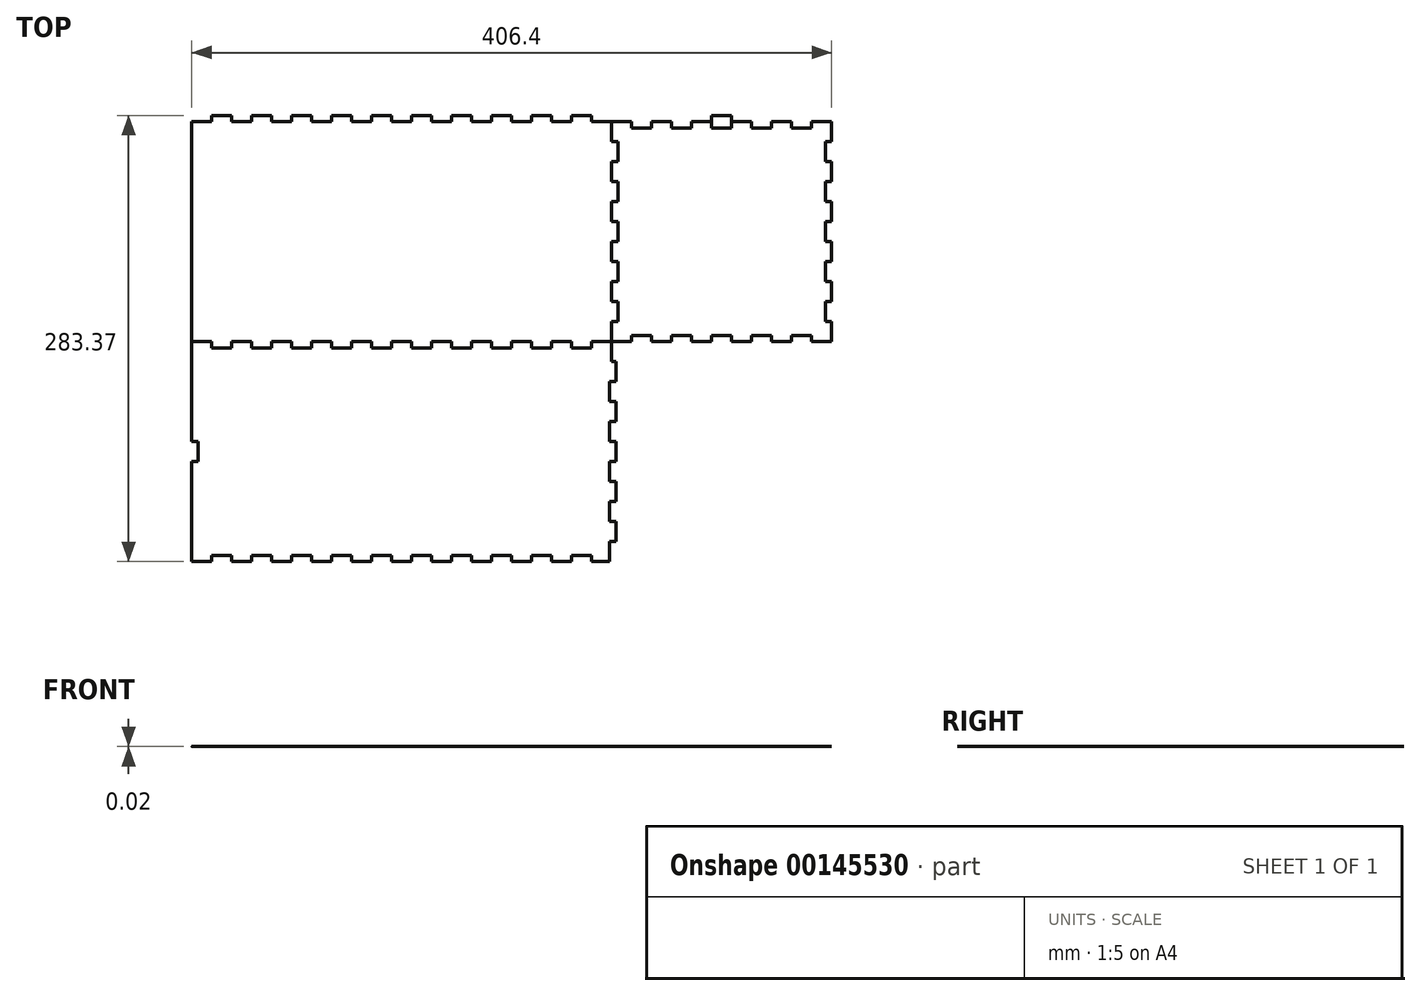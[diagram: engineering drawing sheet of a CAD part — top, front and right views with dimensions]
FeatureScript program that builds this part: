
annotation { "Feature Type Name" : "Feature", "Feature Type Description" : "" }
export const myFeature = defineFeature(function(context is Context, id is Id, definition is map)
    precondition{}
    {
        {
            var Q0;
            Q0=qCreatedBy(makeId("Top.planeOp"),FACE);
            var sketch = newSketch(context, id + "F0", { "sketchPlane" : qUnion([Q0])});
            skLineSegment(sketch, "E0", {"start": v(70.3, -71.79) * mm, "end": v(70.3, -59.09) * mm});
            skLineSegment(sketch, "E1.top", {"start": v(57.6, -67.82) * mm, "end": v(57.6, -71.79) * mm});
            skLineSegment(sketch, "E1.right", {"start": v(70.3, -71.79) * mm, "end": v(57.6, -71.79) * mm});
            skLineSegment(sketch, "E2.0.1.1", {"start": v(44.9, -67.82) * mm, "end": v(44.9, -71.79) * mm});
            skLineSegment(sketch, "E2.0.1.2", {"start": v(44.9, -71.79) * mm, "end": v(32.2, -71.79) * mm});
            skLineSegment(sketch, "E2.0.1.3", {"start": v(32.2, -67.82) * mm, "end": v(32.2, -71.79) * mm});
            skLineSegment(sketch, "E2.0.2.1", {"start": v(19.5, -67.82) * mm, "end": v(19.5, -71.79) * mm});
            skLineSegment(sketch, "E2.0.2.2", {"start": v(19.5, -71.79) * mm, "end": v(6.8, -71.79) * mm});
            skLineSegment(sketch, "E2.0.2.3", {"start": v(6.8, -67.82) * mm, "end": v(6.8, -71.79) * mm});
            skLineSegment(sketch, "E2.0.3.1", {"start": v(-5.9, -67.82) * mm, "end": v(-5.9, -71.79) * mm});
            skLineSegment(sketch, "E2.0.3.2", {"start": v(-5.9, -71.79) * mm, "end": v(-18.6, -71.79) * mm});
            skLineSegment(sketch, "E2.0.3.3", {"start": v(-18.6, -67.82) * mm, "end": v(-18.6, -71.79) * mm});
            skLineSegment(sketch, "E2.0.4.1", {"start": v(-31.3, -67.82) * mm, "end": v(-31.3, -71.79) * mm});
            skLineSegment(sketch, "E2.0.4.2", {"start": v(-31.3, -71.79) * mm, "end": v(-44, -71.79) * mm});
            skLineSegment(sketch, "E2.0.4.3", {"start": v(-44, -67.82) * mm, "end": v(-44, -71.79) * mm});
            skLineSegment(sketch, "E3", {"start": v(-44, -67.82) * mm, "end": v(-56.7, -67.82) * mm});
            skLineSegment(sketch, "E4", {"start": v(-31.3, -67.82) * mm, "end": v(-18.6, -67.82) * mm});
            skLineSegment(sketch, "E5", {"start": v(-5.9, -67.82) * mm, "end": v(6.8, -67.82) * mm});
            skLineSegment(sketch, "E6", {"start": v(19.5, -67.82) * mm, "end": v(32.2, -67.82) * mm});
            skLineSegment(sketch, "E7", {"start": v(44.9, -67.82) * mm, "end": v(57.6, -67.82) * mm});
            skLineSegment(sketch, "E8.MirrorCS", {"start": v(70.3, -46.39) * mm, "end": v(70.3, -33.69) * mm});
            skLineSegment(sketch, "E9.MirrorCS", {"start": v(66.34, -46.39) * mm, "end": v(66.34, -59.09) * mm});
            skLineSegment(sketch, "E10.MirrorCS", {"start": v(70.3, -33.69) * mm, "end": v(66.34, -33.69) * mm});
            skLineSegment(sketch, "E11.MirrorCS", {"start": v(66.34, -20.99) * mm, "end": v(66.34, -33.69) * mm});
            skLineSegment(sketch, "E12.MirrorCS", {"start": v(70.3, 4.41) * mm, "end": v(66.34, 4.41) * mm});
            skLineSegment(sketch, "E13.MirrorCS", {"start": v(70.3, 29.81) * mm, "end": v(66.34, 29.81) * mm});
            skLineSegment(sketch, "E14.MirrorCS", {"start": v(70.3, -46.39) * mm, "end": v(66.34, -46.39) * mm});
            skLineSegment(sketch, "E15.MirrorCS", {"start": v(70.3, 29.81) * mm, "end": v(70.3, 42.51) * mm});
            skLineSegment(sketch, "E16.MirrorCS", {"start": v(70.3, -20.99) * mm, "end": v(66.34, -20.99) * mm});
            skLineSegment(sketch, "E17.MirrorCS", {"start": v(66.34, 29.81) * mm, "end": v(66.34, 17.11) * mm});
            skLineSegment(sketch, "E18.MirrorCS", {"start": v(70.3, 42.51) * mm, "end": v(66.34, 42.51) * mm});
            skLineSegment(sketch, "E19.MirrorCS", {"start": v(70.3, 17.11) * mm, "end": v(66.34, 17.11) * mm});
            skLineSegment(sketch, "E20.MirrorCS", {"start": v(70.3, 55.21) * mm, "end": v(66.34, 55.21) * mm});
            skLineSegment(sketch, "E21.MirrorCS", {"start": v(70.3, -8.29) * mm, "end": v(66.34, -8.29) * mm});
            skLineSegment(sketch, "E22.MirrorCS", {"start": v(70.3, -59.09) * mm, "end": v(66.34, -59.09) * mm});
            skLineSegment(sketch, "E23.MirrorCS", {"start": v(70.3, 4.41) * mm, "end": v(70.3, 17.11) * mm});
            skLineSegment(sketch, "E24.MirrorCS", {"start": v(66.34, 55.21) * mm, "end": v(66.34, 42.51) * mm});
            skLineSegment(sketch, "E25.MirrorCS", {"start": v(66.34, 4.41) * mm, "end": v(66.34, -8.29) * mm});
            skLineSegment(sketch, "E26.MirrorCS", {"start": v(70.3, -20.99) * mm, "end": v(70.3, -8.29) * mm});
            skLineSegment(sketch, "E27", {"start": v(70.3, 67.91) * mm, "end": v(70.3, 55.21) * mm});
            skLineSegment(sketch, "E28.MirrorCS", {"start": v(70.3, -33.69) * mm, "end": v(70.3, -46.39) * mm});
            skLineSegment(sketch, "E29.MirrorCS", {"start": v(66.34, 42.51) * mm, "end": v(66.34, 55.21) * mm});
            skLineSegment(sketch, "E30.MirrorCS", {"start": v(66.34, 17.11) * mm, "end": v(66.34, 29.81) * mm});
            skLineSegment(sketch, "E31.MirrorCS", {"start": v(66.34, -33.69) * mm, "end": v(66.34, -20.99) * mm});
            skLineSegment(sketch, "E32.MirrorCS", {"start": v(70.3, -8.29) * mm, "end": v(70.3, -20.99) * mm});
            skLineSegment(sketch, "E33.MirrorCS", {"start": v(66.34, -8.29) * mm, "end": v(66.34, 4.41) * mm});
            skLineSegment(sketch, "E34.MirrorCS", {"start": v(70.3, 17.11) * mm, "end": v(70.3, 4.41) * mm});
            skLineSegment(sketch, "E35.MirrorCS", {"start": v(66.34, -59.09) * mm, "end": v(66.34, -46.39) * mm});
            skLineSegment(sketch, "E36.MirrorCS", {"start": v(70.3, 42.51) * mm, "end": v(70.3, 29.81) * mm});
            skLineSegment(sketch, "E37", {"start": v(-56.7, -67.82) * mm, "end": v(-56.7, -71.79) * mm});
            skLineSegment(sketch, "E38", {"start": v(-56.7, -71.79) * mm, "end": v(-69.4, -71.79) * mm});
            skLineSegment(sketch, "E39.MirrorCS", {"start": v(-69.4, 17.11) * mm, "end": v(-65.42, 17.11) * mm});
            skLineSegment(sketch, "E40.MirrorCS", {"start": v(-69.4, 29.81) * mm, "end": v(-65.42, 29.81) * mm});
            skLineSegment(sketch, "E41.MirrorCS", {"start": v(-69.4, -33.69) * mm, "end": v(-65.42, -33.69) * mm});
            skLineSegment(sketch, "E42.MirrorCS", {"start": v(-69.4, 42.51) * mm, "end": v(-65.42, 42.51) * mm});
            skLineSegment(sketch, "E43.MirrorCS", {"start": v(-69.4, -8.29) * mm, "end": v(-65.42, -8.29) * mm});
            skLineSegment(sketch, "E44.MirrorCS", {"start": v(-69.4, -46.39) * mm, "end": v(-65.42, -46.39) * mm});
            skLineSegment(sketch, "E45.MirrorCS", {"start": v(-69.4, -20.99) * mm, "end": v(-65.42, -20.99) * mm});
            skLineSegment(sketch, "E46.MirrorCS", {"start": v(-69.4, 4.41) * mm, "end": v(-65.42, 4.41) * mm});
            skLineSegment(sketch, "E47.MirrorCS", {"start": v(-69.4, -59.09) * mm, "end": v(-65.42, -59.09) * mm});
            skLineSegment(sketch, "E48.MirrorCS", {"start": v(-69.4, 55.21) * mm, "end": v(-65.42, 55.21) * mm});
            skLineSegment(sketch, "E49.MirrorCS", {"start": v(-69.4, -8.29) * mm, "end": v(-69.4, -20.99) * mm});
            skLineSegment(sketch, "E50.MirrorCS", {"start": v(-69.4, -46.39) * mm, "end": v(-69.4, -33.69) * mm});
            skLineSegment(sketch, "E51.MirrorCS", {"start": v(-65.42, -59.09) * mm, "end": v(-65.42, -46.39) * mm});
            skLineSegment(sketch, "E52.MirrorCS", {"start": v(-69.4, -71.79) * mm, "end": v(-69.4, -59.09) * mm});
            skLineSegment(sketch, "E53.MirrorCS", {"start": v(-69.4, 29.81) * mm, "end": v(-69.4, 42.51) * mm});
            skLineSegment(sketch, "E54.MirrorCS", {"start": v(-65.42, -8.29) * mm, "end": v(-65.42, 4.41) * mm});
            skLineSegment(sketch, "E55.MirrorCS", {"start": v(-65.42, -20.99) * mm, "end": v(-65.42, -33.69) * mm});
            skLineSegment(sketch, "E56.MirrorCS", {"start": v(-65.42, 29.81) * mm, "end": v(-65.42, 17.11) * mm});
            skLineSegment(sketch, "E57.MirrorCS", {"start": v(-69.4, 4.41) * mm, "end": v(-69.4, 17.11) * mm});
            skLineSegment(sketch, "E58.MirrorCS", {"start": v(-69.4, 67.91) * mm, "end": v(-69.4, 55.21) * mm});
            skLineSegment(sketch, "E59.MirrorCS", {"start": v(-65.42, 42.51) * mm, "end": v(-65.42, 55.21) * mm});
            skLineSegment(sketch, "E60.MirrorCS", {"start": v(-69.4, -33.69) * mm, "end": v(-69.4, -46.39) * mm});
            skLineSegment(sketch, "E61.MirrorCS", {"start": v(-69.4, 17.11) * mm, "end": v(-69.4, 4.41) * mm});
            skLineSegment(sketch, "E62.MirrorCS", {"start": v(-65.42, 4.41) * mm, "end": v(-65.42, -8.29) * mm});
            skLineSegment(sketch, "E63.MirrorCS", {"start": v(-69.4, 42.51) * mm, "end": v(-69.4, 29.81) * mm});
            skLineSegment(sketch, "E64.MirrorCS", {"start": v(-65.42, 17.11) * mm, "end": v(-65.42, 29.81) * mm});
            skLineSegment(sketch, "E65.MirrorCS", {"start": v(-69.4, -20.99) * mm, "end": v(-69.4, -8.29) * mm});
            skLineSegment(sketch, "E66.MirrorCS", {"start": v(-65.42, 55.21) * mm, "end": v(-65.42, 42.51) * mm});
            skLineSegment(sketch, "E67.MirrorCS", {"start": v(-65.42, -33.69) * mm, "end": v(-65.42, -20.99) * mm});
            skLineSegment(sketch, "E68.MirrorCS", {"start": v(-65.42, -46.39) * mm, "end": v(-65.42, -59.09) * mm});
            skLineSegment(sketch, "E69.MirrorCS", {"start": v(-69.4, -71.79) * mm, "end": v(-56.7, -71.79) * mm});
            skLineSegment(sketch, "E70.MirrorCS", {"start": v(-31.3, 63.95) * mm, "end": v(-31.3, 67.91) * mm});
            skLineSegment(sketch, "E71.MirrorCS", {"start": v(-5.9, 63.95) * mm, "end": v(-5.9, 67.91) * mm});
            skLineSegment(sketch, "E72.MirrorCS", {"start": v(6.8, 63.95) * mm, "end": v(6.8, 67.91) * mm});
            skLineSegment(sketch, "E73.MirrorCS", {"start": v(-44, 63.95) * mm, "end": v(-44, 67.91) * mm});
            skLineSegment(sketch, "E74.MirrorCS", {"start": v(57.6, 63.95) * mm, "end": v(57.6, 67.91) * mm});
            skLineSegment(sketch, "E75.MirrorCS", {"start": v(32.2, 63.95) * mm, "end": v(32.2, 67.91) * mm});
            skLineSegment(sketch, "E76.MirrorCS", {"start": v(19.5, 63.95) * mm, "end": v(19.5, 67.91) * mm});
            skLineSegment(sketch, "E77.MirrorCS", {"start": v(44.9, 63.95) * mm, "end": v(44.9, 67.91) * mm});
            skLineSegment(sketch, "E78.MirrorCS", {"start": v(-56.7, 63.95) * mm, "end": v(-56.7, 67.91) * mm});
            skLineSegment(sketch, "E79.MirrorCS", {"start": v(-18.6, 63.95) * mm, "end": v(-18.6, 67.91) * mm});
            skLineSegment(sketch, "E80.MirrorCS", {"start": v(-56.7, 67.91) * mm, "end": v(-69.4, 67.91) * mm});
            skLineSegment(sketch, "E81.MirrorCS", {"start": v(-69.4, 67.91) * mm, "end": v(-56.7, 67.91) * mm});
            skLineSegment(sketch, "E82.MirrorCS", {"start": v(-44, 63.95) * mm, "end": v(-56.7, 63.95) * mm});
            skLineSegment(sketch, "E83.MirrorCS", {"start": v(-31.3, 67.91) * mm, "end": v(-44, 67.91) * mm});
            skLineSegment(sketch, "E84.MirrorCS", {"start": v(44.9, 63.95) * mm, "end": v(57.6, 63.95) * mm});
            skLineSegment(sketch, "E85.MirrorCS", {"start": v(-5.9, 67.91) * mm, "end": v(-18.6, 67.91) * mm});
            skLineSegment(sketch, "E86.MirrorCS", {"start": v(19.5, 63.95) * mm, "end": v(32.2, 63.95) * mm});
            skLineSegment(sketch, "E87.MirrorCS", {"start": v(44.9, 67.91) * mm, "end": v(32.2, 67.91) * mm});
            skLineSegment(sketch, "E88.MirrorCS", {"start": v(70.3, 67.91) * mm, "end": v(57.6, 67.91) * mm});
            skLineSegment(sketch, "E89.MirrorCS", {"start": v(-31.3, 63.95) * mm, "end": v(-18.6, 63.95) * mm});
            skLineSegment(sketch, "E90.MirrorCS", {"start": v(-5.9, 63.95) * mm, "end": v(6.8, 63.95) * mm});
            skLineSegment(sketch, "E91.MirrorCS", {"start": v(19.5, 67.91) * mm, "end": v(6.8, 67.91) * mm});
            skSolve(sketch);
        }
        {
            var Q0;
            Q0 = qSketchRegion(id + "F0", true);
            extrude(context, id + "F1", {"entities" : qUnion([Q0]), "depth" : 5 / 812.8 * mm});
        }
        {
            var Q0;
            Q0=makeQuery(id+"F1.opExtrude","CAP_FACE",FACE,{"disambiguationData":[OSD([sQuery(id+"F0.wireOp",EDGE,"E0"),sQuery(id+"F0.wireOp",EDGE,"E1.top"),sQuery(id+"F0.wireOp",EDGE,"E1.right"),sQuery(id+"F0.wireOp",EDGE,"E2.0.1.1"),sQuery(id+"F0.wireOp",EDGE,"E2.0.1.2"),sQuery(id+"F0.wireOp",EDGE,"E2.0.1.3"),sQuery(id+"F0.wireOp",EDGE,"E2.0.2.1"),sQuery(id+"F0.wireOp",EDGE,"E2.0.2.2"),sQuery(id+"F0.wireOp",EDGE,"E2.0.2.3"),sQuery(id+"F0.wireOp",EDGE,"E2.0.3.1"),sQuery(id+"F0.wireOp",EDGE,"E2.0.3.2"),sQuery(id+"F0.wireOp",EDGE,"E2.0.3.3"),sQuery(id+"F0.wireOp",EDGE,"E2.0.4.1"),sQuery(id+"F0.wireOp",EDGE,"E2.0.4.2"),sQuery(id+"F0.wireOp",EDGE,"E2.0.4.3"),sQuery(id+"F0.wireOp",EDGE,"E3"),sQuery(id+"F0.wireOp",EDGE,"E4"),sQuery(id+"F0.wireOp",EDGE,"E5"),sQuery(id+"F0.wireOp",EDGE,"E6"),sQuery(id+"F0.wireOp",EDGE,"E7"),sQuery(id+"F0.wireOp",EDGE,"E27"),sQuery(id+"F0.wireOp",EDGE,"E28.MirrorCS"),sQuery(id+"F0.wireOp",EDGE,"E21.MirrorCS"),sQuery(id+"F0.wireOp",EDGE,"E14.MirrorCS"),sQuery(id+"F0.wireOp",EDGE,"E29.MirrorCS"),sQuery(id+"F0.wireOp",EDGE,"E30.MirrorCS"),sQuery(id+"F0.wireOp",EDGE,"E31.MirrorCS"),sQuery(id+"F0.wireOp",EDGE,"E13.MirrorCS"),sQuery(id+"F0.wireOp",EDGE,"E20.MirrorCS"),sQuery(id+"F0.wireOp",EDGE,"E10.MirrorCS"),sQuery(id+"F0.wireOp",EDGE,"E32.MirrorCS"),sQuery(id+"F0.wireOp",EDGE,"E19.MirrorCS"),sQuery(id+"F0.wireOp",EDGE,"E33.MirrorCS"),sQuery(id+"F0.wireOp",EDGE,"E22.MirrorCS"),sQuery(id+"F0.wireOp",EDGE,"E12.MirrorCS"),sQuery(id+"F0.wireOp",EDGE,"E34.MirrorCS"),sQuery(id+"F0.wireOp",EDGE,"E16.MirrorCS"),sQuery(id+"F0.wireOp",EDGE,"E35.MirrorCS"),sQuery(id+"F0.wireOp",EDGE,"E36.MirrorCS"),sQuery(id+"F0.wireOp",EDGE,"E18.MirrorCS"),sQuery(id+"F0.wireOp",EDGE,"E37"),sQuery(id+"F0.wireOp",EDGE,"E45.MirrorCS"),sQuery(id+"F0.wireOp",EDGE,"E41.MirrorCS"),sQuery(id+"F0.wireOp",EDGE,"E43.MirrorCS"),sQuery(id+"F0.wireOp",EDGE,"E40.MirrorCS"),sQuery(id+"F0.wireOp",EDGE,"E44.MirrorCS"),sQuery(id+"F0.wireOp",EDGE,"E39.MirrorCS"),sQuery(id+"F0.wireOp",EDGE,"E42.MirrorCS"),sQuery(id+"F0.wireOp",EDGE,"E46.MirrorCS"),sQuery(id+"F0.wireOp",EDGE,"E47.MirrorCS"),sQuery(id+"F0.wireOp",EDGE,"E48.MirrorCS"),sQuery(id+"F0.wireOp",EDGE,"E52.MirrorCS"),sQuery(id+"F0.wireOp",EDGE,"E58.MirrorCS"),sQuery(id+"F0.wireOp",EDGE,"E60.MirrorCS"),sQuery(id+"F0.wireOp",EDGE,"E61.MirrorCS"),sQuery(id+"F0.wireOp",EDGE,"E62.MirrorCS"),sQuery(id+"F0.wireOp",EDGE,"E63.MirrorCS"),sQuery(id+"F0.wireOp",EDGE,"E64.MirrorCS"),sQuery(id+"F0.wireOp",EDGE,"E65.MirrorCS"),sQuery(id+"F0.wireOp",EDGE,"E66.MirrorCS"),sQuery(id+"F0.wireOp",EDGE,"E67.MirrorCS"),sQuery(id+"F0.wireOp",EDGE,"E68.MirrorCS"),sQuery(id+"F0.wireOp",EDGE,"E69.MirrorCS"),sQuery(id+"F0.wireOp",EDGE,"E70.MirrorCS"),sQuery(id+"F0.wireOp",EDGE,"E71.MirrorCS"),sQuery(id+"F0.wireOp",EDGE,"E72.MirrorCS"),sQuery(id+"F0.wireOp",EDGE,"E73.MirrorCS"),sQuery(id+"F0.wireOp",EDGE,"E74.MirrorCS"),sQuery(id+"F0.wireOp",EDGE,"E75.MirrorCS"),sQuery(id+"F0.wireOp",EDGE,"E76.MirrorCS"),sQuery(id+"F0.wireOp",EDGE,"E77.MirrorCS"),sQuery(id+"F0.wireOp",EDGE,"E78.MirrorCS"),sQuery(id+"F0.wireOp",EDGE,"E79.MirrorCS"),sQuery(id+"F0.wireOp",EDGE,"E81.MirrorCS"),sQuery(id+"F0.wireOp",EDGE,"E82.MirrorCS"),sQuery(id+"F0.wireOp",EDGE,"E83.MirrorCS"),sQuery(id+"F0.wireOp",EDGE,"E84.MirrorCS"),sQuery(id+"F0.wireOp",EDGE,"E85.MirrorCS"),sQuery(id+"F0.wireOp",EDGE,"E86.MirrorCS"),sQuery(id+"F0.wireOp",EDGE,"E87.MirrorCS"),sQuery(id+"F0.wireOp",EDGE,"E88.MirrorCS"),sQuery(id+"F0.wireOp",EDGE,"E89.MirrorCS"),sQuery(id+"F0.wireOp",EDGE,"E90.MirrorCS"),sQuery(id+"F0.wireOp",EDGE,"E91.MirrorCS")])],"isStart":true});
            var sketch = newSketch(context, id + "F2", { "sketchPlane" : qUnion([Q0])});
            skLineSegment(sketch, "E92.0", {"start": v(-69.4, -67.91) * mm, "end": v(-69.4, -55.21) * mm});
            skLineSegment(sketch, "E92.1", {"start": v(-69.4, -55.21) * mm, "end": v(-65.42, -55.21) * mm});
            skLineSegment(sketch, "E92.2", {"start": v(-65.42, -55.21) * mm, "end": v(-65.42, -42.51) * mm});
            skLineSegment(sketch, "E92.3", {"start": v(-69.4, -42.51) * mm, "end": v(-65.42, -42.51) * mm});
            skLineSegment(sketch, "E92.4", {"start": v(-69.4, -42.51) * mm, "end": v(-69.4, -29.81) * mm});
            skLineSegment(sketch, "E92.5", {"start": v(-69.4, -29.81) * mm, "end": v(-65.42, -29.81) * mm});
            skLineSegment(sketch, "E92.6", {"start": v(-65.42, -17.11) * mm, "end": v(-65.42, -29.81) * mm});
            skLineSegment(sketch, "E92.7", {"start": v(-69.4, -17.11) * mm, "end": v(-65.42, -17.11) * mm});
            skLineSegment(sketch, "E92.8", {"start": v(-69.4, -17.11) * mm, "end": v(-69.4, -4.41) * mm});
            skLineSegment(sketch, "E92.9", {"start": v(-69.4, -4.41) * mm, "end": v(-65.42, -4.41) * mm});
            skLineSegment(sketch, "E92.10", {"start": v(-65.42, -4.41) * mm, "end": v(-65.42, 8.29) * mm});
            skLineSegment(sketch, "E92.11", {"start": v(-69.4, 46.39) * mm, "end": v(-65.42, 46.39) * mm});
            skLineSegment(sketch, "E92.12", {"start": v(-65.42, 46.39) * mm, "end": v(-65.42, 59.09) * mm});
            skLineSegment(sketch, "E92.13", {"start": v(-69.4, 59.09) * mm, "end": v(-65.42, 59.09) * mm});
            skLineSegment(sketch, "E92.14", {"start": v(-69.4, 71.79) * mm, "end": v(-69.4, 59.09) * mm});
            skLineSegment(sketch, "E92.15", {"start": v(-69.4, 33.69) * mm, "end": v(-69.4, 46.39) * mm});
            skLineSegment(sketch, "E92.16", {"start": v(-69.4, 33.69) * mm, "end": v(-65.42, 33.69) * mm});
            skLineSegment(sketch, "E92.17", {"start": v(-65.42, 33.69) * mm, "end": v(-65.42, 20.99) * mm});
            skLineSegment(sketch, "E92.18", {"start": v(-69.4, 20.99) * mm, "end": v(-65.42, 20.99) * mm});
            skLineSegment(sketch, "E92.19", {"start": v(-69.4, 20.99) * mm, "end": v(-69.4, 8.29) * mm});
            skLineSegment(sketch, "E92.20", {"start": v(-69.4, 8.29) * mm, "end": v(-65.42, 8.29) * mm});
            skLineSegment(sketch, "E93.right", {"start": v(-336.1, 71.79) * mm, "end": v(-336.1, -67.91) * mm});
            skLineSegment(sketch, "E94.1.0.0", {"start": v(-132.9, -67.91) * mm, "end": v(-132.9, -71.88) * mm});
            skLineSegment(sketch, "E94.1.0.1", {"start": v(-107.5, -67.91) * mm, "end": v(-107.5, -71.88) * mm});
            skLineSegment(sketch, "E94.1.0.2", {"start": v(-107.5, -71.88) * mm, "end": v(-120.2, -71.88) * mm});
            skLineSegment(sketch, "E94.1.0.3", {"start": v(-82.1, -67.91) * mm, "end": v(-82.1, -71.88) * mm});
            skLineSegment(sketch, "E94.1.0.4", {"start": v(-107.5, -67.91) * mm, "end": v(-94.8, -67.91) * mm});
            skLineSegment(sketch, "E94.1.0.6", {"start": v(-196.4, -67.91) * mm, "end": v(-196.4, -71.88) * mm});
            skLineSegment(sketch, "E94.1.0.7", {"start": v(-196.4, -71.88) * mm, "end": v(-183.7, -71.88) * mm});
            skLineSegment(sketch, "E94.1.0.8", {"start": v(-183.7, -67.91) * mm, "end": v(-183.7, -71.88) * mm});
            skLineSegment(sketch, "E94.1.0.9", {"start": v(-183.7, -67.91) * mm, "end": v(-171, -67.91) * mm});
            skLineSegment(sketch, "E94.1.0.10", {"start": v(-171, -67.91) * mm, "end": v(-171, -71.88) * mm});
            skLineSegment(sketch, "E94.1.0.11", {"start": v(-158.3, -71.88) * mm, "end": v(-171, -71.88) * mm});
            skLineSegment(sketch, "E94.1.0.12", {"start": v(-158.3, -67.91) * mm, "end": v(-158.3, -71.88) * mm});
            skLineSegment(sketch, "E94.1.0.13", {"start": v(-158.3, -67.91) * mm, "end": v(-145.6, -67.91) * mm});
            skLineSegment(sketch, "E94.1.0.14", {"start": v(-145.6, -71.88) * mm, "end": v(-132.9, -71.88) * mm});
            skLineSegment(sketch, "E94.1.0.15", {"start": v(-145.6, -67.91) * mm, "end": v(-145.6, -71.88) * mm});
            skLineSegment(sketch, "E94.1.0.16", {"start": v(-94.8, -67.91) * mm, "end": v(-94.8, -71.88) * mm});
            skLineSegment(sketch, "E94.1.0.17", {"start": v(-94.8, -71.88) * mm, "end": v(-82.1, -71.88) * mm});
            skLineSegment(sketch, "E94.1.0.18", {"start": v(-120.2, -67.91) * mm, "end": v(-120.2, -71.88) * mm});
            skLineSegment(sketch, "E94.1.0.19", {"start": v(-120.2, -67.91) * mm, "end": v(-132.9, -67.91) * mm});
            skLineSegment(sketch, "E95", {"start": v(-69.4, -67.91) * mm, "end": v(-82.1, -67.91) * mm});
            skLineSegment(sketch, "E96", {"start": v(-209.1, 71.79) * mm, "end": v(-202.74, 71.79) * mm});
            skLineSegment(sketch, "E97.MirrorCS", {"start": v(-323.4, -67.91) * mm, "end": v(-323.4, -71.88) * mm});
            skLineSegment(sketch, "E98.MirrorCS", {"start": v(-247.2, -67.91) * mm, "end": v(-247.2, -71.88) * mm});
            skLineSegment(sketch, "E99.MirrorCS", {"start": v(-298, -67.91) * mm, "end": v(-298, -71.88) * mm});
            skLineSegment(sketch, "E100.MirrorCS", {"start": v(-272.6, -67.91) * mm, "end": v(-272.6, -71.88) * mm});
            skLineSegment(sketch, "E101.MirrorCS", {"start": v(-234.5, -67.91) * mm, "end": v(-234.5, -71.88) * mm});
            skLineSegment(sketch, "E102.MirrorCS", {"start": v(-285.3, -67.91) * mm, "end": v(-285.3, -71.88) * mm});
            skLineSegment(sketch, "E103.MirrorCS", {"start": v(-259.9, -67.91) * mm, "end": v(-259.9, -71.88) * mm});
            skLineSegment(sketch, "E104.MirrorCS", {"start": v(-221.8, -67.91) * mm, "end": v(-221.8, -71.88) * mm});
            skLineSegment(sketch, "E105.MirrorCS", {"start": v(-310.7, -67.91) * mm, "end": v(-310.7, -71.88) * mm});
            skLineSegment(sketch, "E106.MirrorCS", {"start": v(-209.1, -67.91) * mm, "end": v(-209.1, -71.88) * mm});
            skLineSegment(sketch, "E107.MirrorCS", {"start": v(-336.1, -67.91) * mm, "end": v(-323.4, -67.91) * mm});
            skLineSegment(sketch, "E108.MirrorCS", {"start": v(-209.1, -71.88) * mm, "end": v(-221.8, -71.88) * mm});
            skLineSegment(sketch, "E109.MirrorCS", {"start": v(-285.3, -67.91) * mm, "end": v(-272.6, -67.91) * mm});
            skLineSegment(sketch, "E110.MirrorCS", {"start": v(-298, -71.88) * mm, "end": v(-285.3, -71.88) * mm});
            skLineSegment(sketch, "E111.MirrorCS", {"start": v(-247.2, -67.91) * mm, "end": v(-259.9, -67.91) * mm});
            skLineSegment(sketch, "E112.MirrorCS", {"start": v(-298, -67.91) * mm, "end": v(-310.7, -67.91) * mm});
            skLineSegment(sketch, "E113.MirrorCS", {"start": v(-310.7, -71.88) * mm, "end": v(-323.4, -71.88) * mm});
            skLineSegment(sketch, "E114.MirrorCS", {"start": v(-247.2, -71.88) * mm, "end": v(-234.5, -71.88) * mm});
            skLineSegment(sketch, "E115.MirrorCS", {"start": v(-259.9, -71.88) * mm, "end": v(-272.6, -71.88) * mm});
            skLineSegment(sketch, "E116.MirrorCS", {"start": v(-221.8, -67.91) * mm, "end": v(-234.5, -67.91) * mm});
            skLineSegment(sketch, "E117", {"start": v(-209.1, -67.91) * mm, "end": v(-196.4, -67.91) * mm});
            skLineSegment(sketch, "E118.MirrorCS", {"start": v(-209.1, 71.79) * mm, "end": v(-209.1, 75.75) * mm});
            skLineSegment(sketch, "E119.MirrorCS", {"start": v(-94.8, 71.79) * mm, "end": v(-94.8, 75.75) * mm});
            skLineSegment(sketch, "E120.MirrorCS", {"start": v(-183.7, 71.79) * mm, "end": v(-183.7, 75.75) * mm});
            skLineSegment(sketch, "E121.MirrorCS", {"start": v(-298, 71.79) * mm, "end": v(-298, 75.75) * mm});
            skLineSegment(sketch, "E122.MirrorCS", {"start": v(-145.6, 71.79) * mm, "end": v(-145.6, 75.75) * mm});
            skLineSegment(sketch, "E123.MirrorCS", {"start": v(-158.3, 71.79) * mm, "end": v(-158.3, 75.75) * mm});
            skLineSegment(sketch, "E124.MirrorCS", {"start": v(-285.3, 71.79) * mm, "end": v(-285.3, 75.75) * mm});
            skLineSegment(sketch, "E125.MirrorCS", {"start": v(-82.1, 71.79) * mm, "end": v(-82.1, 75.75) * mm});
            skLineSegment(sketch, "E126.MirrorCS", {"start": v(-259.9, 71.79) * mm, "end": v(-259.9, 75.75) * mm});
            skLineSegment(sketch, "E127.MirrorCS", {"start": v(-196.4, 71.79) * mm, "end": v(-196.4, 75.75) * mm});
            skLineSegment(sketch, "E128.MirrorCS", {"start": v(-221.8, 71.79) * mm, "end": v(-221.8, 75.75) * mm});
            skLineSegment(sketch, "E129.MirrorCS", {"start": v(-132.9, 71.79) * mm, "end": v(-132.9, 75.75) * mm});
            skLineSegment(sketch, "E130.MirrorCS", {"start": v(-120.2, 71.79) * mm, "end": v(-120.2, 75.75) * mm});
            skLineSegment(sketch, "E131.MirrorCS", {"start": v(-107.5, 71.79) * mm, "end": v(-107.5, 75.75) * mm});
            skLineSegment(sketch, "E132.MirrorCS", {"start": v(-171, 71.79) * mm, "end": v(-171, 75.75) * mm});
            skLineSegment(sketch, "E133.MirrorCS", {"start": v(-272.6, 71.79) * mm, "end": v(-272.6, 75.75) * mm});
            skLineSegment(sketch, "E134.MirrorCS", {"start": v(-323.4, 71.79) * mm, "end": v(-323.4, 75.75) * mm});
            skLineSegment(sketch, "E135.MirrorCS", {"start": v(-247.2, 71.79) * mm, "end": v(-247.2, 75.75) * mm});
            skLineSegment(sketch, "E136.MirrorCS", {"start": v(-310.7, 71.79) * mm, "end": v(-310.7, 75.75) * mm});
            skLineSegment(sketch, "E137.MirrorCS", {"start": v(-234.5, 71.79) * mm, "end": v(-234.5, 75.75) * mm});
            skLineSegment(sketch, "E138.MirrorCS", {"start": v(-183.7, 71.79) * mm, "end": v(-171, 71.79) * mm});
            skLineSegment(sketch, "E139.MirrorCS", {"start": v(-221.8, 71.79) * mm, "end": v(-234.5, 71.79) * mm});
            skLineSegment(sketch, "E140.MirrorCS", {"start": v(-336.1, 71.79) * mm, "end": v(-323.4, 71.79) * mm});
            skLineSegment(sketch, "E141.MirrorCS", {"start": v(-209.1, 71.79) * mm, "end": v(-196.4, 71.79) * mm});
            skLineSegment(sketch, "E142.MirrorCS", {"start": v(-285.3, 71.79) * mm, "end": v(-272.6, 71.79) * mm});
            skLineSegment(sketch, "E143.MirrorCS", {"start": v(-120.2, 71.79) * mm, "end": v(-132.9, 71.79) * mm});
            skLineSegment(sketch, "E144.MirrorCS", {"start": v(-107.5, 75.75) * mm, "end": v(-120.2, 75.75) * mm});
            skLineSegment(sketch, "E145.MirrorCS", {"start": v(-298, 75.75) * mm, "end": v(-285.3, 75.75) * mm});
            skLineSegment(sketch, "E146.MirrorCS", {"start": v(-69.4, 71.79) * mm, "end": v(-82.1, 71.79) * mm});
            skLineSegment(sketch, "E147.MirrorCS", {"start": v(-158.3, 71.79) * mm, "end": v(-145.6, 71.79) * mm});
            skLineSegment(sketch, "E148.MirrorCS", {"start": v(-310.7, 75.75) * mm, "end": v(-323.4, 75.75) * mm});
            skLineSegment(sketch, "E149.MirrorCS", {"start": v(-298, 71.79) * mm, "end": v(-310.7, 71.79) * mm});
            skLineSegment(sketch, "E150.MirrorCS", {"start": v(-247.2, 75.75) * mm, "end": v(-234.5, 75.75) * mm});
            skLineSegment(sketch, "E151.MirrorCS", {"start": v(-94.8, 75.75) * mm, "end": v(-82.1, 75.75) * mm});
            skLineSegment(sketch, "E152.MirrorCS", {"start": v(-107.5, 71.79) * mm, "end": v(-94.8, 71.79) * mm});
            skLineSegment(sketch, "E153.MirrorCS", {"start": v(-196.4, 75.75) * mm, "end": v(-183.7, 75.75) * mm});
            skLineSegment(sketch, "E154.MirrorCS", {"start": v(-259.9, 75.75) * mm, "end": v(-272.6, 75.75) * mm});
            skLineSegment(sketch, "E155.MirrorCS", {"start": v(-145.6, 75.75) * mm, "end": v(-132.9, 75.75) * mm});
            skLineSegment(sketch, "E156.MirrorCS", {"start": v(-247.2, 71.79) * mm, "end": v(-259.9, 71.79) * mm});
            skLineSegment(sketch, "E157.MirrorCS", {"start": v(-158.3, 75.75) * mm, "end": v(-171, 75.75) * mm});
            skLineSegment(sketch, "E158.MirrorCS", {"start": v(-209.1, 75.75) * mm, "end": v(-221.8, 75.75) * mm});
            skSolve(sketch);
        }
        {
            var Q0;
            Q0=makeQuery(id+"F2.imprint","IMPRINT",FACE,{"disambiguationData":[TD([[makeQuery(id+"F2.imprint","IMPRINT",EDGE,{"derivedFrom":sQuery(id+"F2.wireOp",EDGE,"E92.0")}),1.0]])]});
            extrude(context, id + "F3", {"entities" : qUnion([Q0]), "depth" : 5 / 812.8 * mm});
        }
        {
            var Q0;
            Q0=makeQuery(id+"F3.opExtrude","CAP_FACE",FACE,{"disambiguationData":[OSD([sQuery(id+"F2.wireOp",EDGE,"E92.0"),sQuery(id+"F2.wireOp",EDGE,"E92.1"),sQuery(id+"F2.wireOp",EDGE,"E92.2"),sQuery(id+"F2.wireOp",EDGE,"E92.3"),sQuery(id+"F2.wireOp",EDGE,"E92.4"),sQuery(id+"F2.wireOp",EDGE,"E92.5"),sQuery(id+"F2.wireOp",EDGE,"E92.6"),sQuery(id+"F2.wireOp",EDGE,"E92.7"),sQuery(id+"F2.wireOp",EDGE,"E92.8"),sQuery(id+"F2.wireOp",EDGE,"E92.9"),sQuery(id+"F2.wireOp",EDGE,"E92.10"),sQuery(id+"F2.wireOp",EDGE,"E92.11"),sQuery(id+"F2.wireOp",EDGE,"E92.12"),sQuery(id+"F2.wireOp",EDGE,"E92.13"),sQuery(id+"F2.wireOp",EDGE,"E92.14"),sQuery(id+"F2.wireOp",EDGE,"E92.15"),sQuery(id+"F2.wireOp",EDGE,"E92.16"),sQuery(id+"F2.wireOp",EDGE,"E92.17"),sQuery(id+"F2.wireOp",EDGE,"E92.18"),sQuery(id+"F2.wireOp",EDGE,"E92.19"),sQuery(id+"F2.wireOp",EDGE,"E92.20"),sQuery(id+"F2.wireOp",EDGE,"E93.right"),sQuery(id+"F2.wireOp",EDGE,"E94.1.0.0"),sQuery(id+"F2.wireOp",EDGE,"E94.1.0.1"),sQuery(id+"F2.wireOp",EDGE,"E94.1.0.2"),sQuery(id+"F2.wireOp",EDGE,"E94.1.0.3"),sQuery(id+"F2.wireOp",EDGE,"E94.1.0.4"),sQuery(id+"F2.wireOp",EDGE,"E94.1.0.6"),sQuery(id+"F2.wireOp",EDGE,"E94.1.0.7"),sQuery(id+"F2.wireOp",EDGE,"E94.1.0.8"),sQuery(id+"F2.wireOp",EDGE,"E94.1.0.9"),sQuery(id+"F2.wireOp",EDGE,"E94.1.0.10"),sQuery(id+"F2.wireOp",EDGE,"E94.1.0.11"),sQuery(id+"F2.wireOp",EDGE,"E94.1.0.12"),sQuery(id+"F2.wireOp",EDGE,"E94.1.0.13"),sQuery(id+"F2.wireOp",EDGE,"E94.1.0.14"),sQuery(id+"F2.wireOp",EDGE,"E94.1.0.15"),sQuery(id+"F2.wireOp",EDGE,"E94.1.0.16"),sQuery(id+"F2.wireOp",EDGE,"E94.1.0.17"),sQuery(id+"F2.wireOp",EDGE,"E94.1.0.18"),sQuery(id+"F2.wireOp",EDGE,"E94.1.0.19"),sQuery(id+"F2.wireOp",EDGE,"E95"),sQuery(id+"F2.wireOp",EDGE,"E97.MirrorCS"),sQuery(id+"F2.wireOp",EDGE,"E98.MirrorCS"),sQuery(id+"F2.wireOp",EDGE,"E99.MirrorCS"),sQuery(id+"F2.wireOp",EDGE,"E100.MirrorCS"),sQuery(id+"F2.wireOp",EDGE,"E101.MirrorCS"),sQuery(id+"F2.wireOp",EDGE,"E102.MirrorCS"),sQuery(id+"F2.wireOp",EDGE,"E103.MirrorCS"),sQuery(id+"F2.wireOp",EDGE,"E104.MirrorCS"),sQuery(id+"F2.wireOp",EDGE,"E105.MirrorCS"),sQuery(id+"F2.wireOp",EDGE,"E106.MirrorCS"),sQuery(id+"F2.wireOp",EDGE,"E107.MirrorCS"),sQuery(id+"F2.wireOp",EDGE,"E108.MirrorCS"),sQuery(id+"F2.wireOp",EDGE,"E109.MirrorCS"),sQuery(id+"F2.wireOp",EDGE,"E110.MirrorCS"),sQuery(id+"F2.wireOp",EDGE,"E111.MirrorCS"),sQuery(id+"F2.wireOp",EDGE,"E112.MirrorCS"),sQuery(id+"F2.wireOp",EDGE,"E113.MirrorCS"),sQuery(id+"F2.wireOp",EDGE,"E114.MirrorCS"),sQuery(id+"F2.wireOp",EDGE,"E115.MirrorCS"),sQuery(id+"F2.wireOp",EDGE,"E116.MirrorCS"),sQuery(id+"F2.wireOp",EDGE,"E117"),sQuery(id+"F2.wireOp",EDGE,"E118.MirrorCS"),sQuery(id+"F2.wireOp",EDGE,"E119.MirrorCS"),sQuery(id+"F2.wireOp",EDGE,"E120.MirrorCS"),sQuery(id+"F2.wireOp",EDGE,"E121.MirrorCS"),sQuery(id+"F2.wireOp",EDGE,"E122.MirrorCS"),sQuery(id+"F2.wireOp",EDGE,"E123.MirrorCS"),sQuery(id+"F2.wireOp",EDGE,"E124.MirrorCS"),sQuery(id+"F2.wireOp",EDGE,"E125.MirrorCS"),sQuery(id+"F2.wireOp",EDGE,"E126.MirrorCS"),sQuery(id+"F2.wireOp",EDGE,"E127.MirrorCS"),sQuery(id+"F2.wireOp",EDGE,"E128.MirrorCS"),sQuery(id+"F2.wireOp",EDGE,"E129.MirrorCS"),sQuery(id+"F2.wireOp",EDGE,"E130.MirrorCS"),sQuery(id+"F2.wireOp",EDGE,"E131.MirrorCS"),sQuery(id+"F2.wireOp",EDGE,"E132.MirrorCS"),sQuery(id+"F2.wireOp",EDGE,"E133.MirrorCS"),sQuery(id+"F2.wireOp",EDGE,"E134.MirrorCS"),sQuery(id+"F2.wireOp",EDGE,"E135.MirrorCS"),sQuery(id+"F2.wireOp",EDGE,"E136.MirrorCS"),sQuery(id+"F2.wireOp",EDGE,"E137.MirrorCS"),sQuery(id+"F2.wireOp",EDGE,"E138.MirrorCS"),sQuery(id+"F2.wireOp",EDGE,"E139.MirrorCS"),sQuery(id+"F2.wireOp",EDGE,"E140.MirrorCS"),sQuery(id+"F2.wireOp",EDGE,"E141.MirrorCS"),sQuery(id+"F2.wireOp",EDGE,"E142.MirrorCS"),sQuery(id+"F2.wireOp",EDGE,"E143.MirrorCS"),sQuery(id+"F2.wireOp",EDGE,"E144.MirrorCS"),sQuery(id+"F2.wireOp",EDGE,"E145.MirrorCS"),sQuery(id+"F2.wireOp",EDGE,"E146.MirrorCS"),sQuery(id+"F2.wireOp",EDGE,"E147.MirrorCS"),sQuery(id+"F2.wireOp",EDGE,"E148.MirrorCS"),sQuery(id+"F2.wireOp",EDGE,"E149.MirrorCS"),sQuery(id+"F2.wireOp",EDGE,"E150.MirrorCS"),sQuery(id+"F2.wireOp",EDGE,"E151.MirrorCS"),sQuery(id+"F2.wireOp",EDGE,"E152.MirrorCS"),sQuery(id+"F2.wireOp",EDGE,"E153.MirrorCS"),sQuery(id+"F2.wireOp",EDGE,"E154.MirrorCS"),sQuery(id+"F2.wireOp",EDGE,"E155.MirrorCS"),sQuery(id+"F2.wireOp",EDGE,"E156.MirrorCS"),sQuery(id+"F2.wireOp",EDGE,"E157.MirrorCS"),sQuery(id+"F2.wireOp",EDGE,"E158.MirrorCS")])],"isStart":true});
            var sketch = newSketch(context, id + "F4", { "sketchPlane" : qUnion([Q0])});
            skLineSegment(sketch, "E159.0", {"start": v(-336.1, -71.79) * mm, "end": v(-323.4, -71.79) * mm});
            skLineSegment(sketch, "E159.1", {"start": v(-323.4, -71.79) * mm, "end": v(-323.4, -75.75) * mm});
            skLineSegment(sketch, "E159.2", {"start": v(-310.7, -75.75) * mm, "end": v(-323.4, -75.75) * mm});
            skLineSegment(sketch, "E159.3", {"start": v(-310.7, -71.79) * mm, "end": v(-310.7, -75.75) * mm});
            skLineSegment(sketch, "E159.4", {"start": v(-298, -71.79) * mm, "end": v(-310.7, -71.79) * mm});
            skLineSegment(sketch, "E159.5", {"start": v(-298, -71.79) * mm, "end": v(-298, -75.75) * mm});
            skLineSegment(sketch, "E159.6", {"start": v(-298, -75.75) * mm, "end": v(-285.3, -75.75) * mm});
            skLineSegment(sketch, "E159.7", {"start": v(-285.3, -71.79) * mm, "end": v(-285.3, -75.75) * mm});
            skLineSegment(sketch, "E159.8", {"start": v(-285.3, -71.79) * mm, "end": v(-272.6, -71.79) * mm});
            skLineSegment(sketch, "E159.9", {"start": v(-272.6, -71.79) * mm, "end": v(-272.6, -75.75) * mm});
            skLineSegment(sketch, "E159.10", {"start": v(-259.9, -75.75) * mm, "end": v(-272.6, -75.75) * mm});
            skLineSegment(sketch, "E159.11", {"start": v(-259.9, -71.79) * mm, "end": v(-259.9, -75.75) * mm});
            skLineSegment(sketch, "E159.12", {"start": v(-247.2, -71.79) * mm, "end": v(-259.9, -71.79) * mm});
            skLineSegment(sketch, "E159.13", {"start": v(-247.2, -71.79) * mm, "end": v(-247.2, -75.75) * mm});
            skLineSegment(sketch, "E159.14", {"start": v(-247.2, -75.75) * mm, "end": v(-234.5, -75.75) * mm});
            skLineSegment(sketch, "E159.15", {"start": v(-234.5, -71.79) * mm, "end": v(-234.5, -75.75) * mm});
            skLineSegment(sketch, "E159.16", {"start": v(-221.8, -71.79) * mm, "end": v(-234.5, -71.79) * mm});
            skLineSegment(sketch, "E159.17", {"start": v(-221.8, -71.79) * mm, "end": v(-221.8, -75.75) * mm});
            skLineSegment(sketch, "E159.18", {"start": v(-209.1, -75.75) * mm, "end": v(-221.8, -75.75) * mm});
            skLineSegment(sketch, "E159.19", {"start": v(-132.9, -71.79) * mm, "end": v(-132.9, -75.75) * mm});
            skLineSegment(sketch, "E159.20", {"start": v(-120.2, -71.79) * mm, "end": v(-132.9, -71.79) * mm});
            skLineSegment(sketch, "E159.21", {"start": v(-120.2, -71.79) * mm, "end": v(-120.2, -75.75) * mm});
            skLineSegment(sketch, "E159.22", {"start": v(-107.5, -75.75) * mm, "end": v(-120.2, -75.75) * mm});
            skLineSegment(sketch, "E159.23", {"start": v(-107.5, -71.79) * mm, "end": v(-107.5, -75.75) * mm});
            skLineSegment(sketch, "E159.24", {"start": v(-107.5, -71.79) * mm, "end": v(-94.8, -71.79) * mm});
            skLineSegment(sketch, "E159.25", {"start": v(-69.4, -71.79) * mm, "end": v(-82.1, -71.79) * mm});
            skLineSegment(sketch, "E159.26", {"start": v(-82.1, -71.79) * mm, "end": v(-82.1, -75.75) * mm});
            skLineSegment(sketch, "E159.27", {"start": v(-94.8, -75.75) * mm, "end": v(-82.1, -75.75) * mm});
            skLineSegment(sketch, "E159.28", {"start": v(-94.8, -71.79) * mm, "end": v(-94.8, -75.75) * mm});
            skLineSegment(sketch, "E159.29", {"start": v(-145.6, -75.75) * mm, "end": v(-132.9, -75.75) * mm});
            skLineSegment(sketch, "E159.30", {"start": v(-145.6, -71.79) * mm, "end": v(-145.6, -75.75) * mm});
            skLineSegment(sketch, "E159.31", {"start": v(-158.3, -71.79) * mm, "end": v(-145.6, -71.79) * mm});
            skLineSegment(sketch, "E159.32", {"start": v(-158.3, -71.79) * mm, "end": v(-158.3, -75.75) * mm});
            skLineSegment(sketch, "E159.33", {"start": v(-158.3, -75.75) * mm, "end": v(-171, -75.75) * mm});
            skLineSegment(sketch, "E159.34", {"start": v(-171, -71.79) * mm, "end": v(-171, -75.75) * mm});
            skLineSegment(sketch, "E159.35", {"start": v(-183.7, -71.79) * mm, "end": v(-171, -71.79) * mm});
            skLineSegment(sketch, "E159.36", {"start": v(-183.7, -71.79) * mm, "end": v(-183.7, -75.75) * mm});
            skLineSegment(sketch, "E159.37", {"start": v(-196.4, -75.75) * mm, "end": v(-183.7, -75.75) * mm});
            skLineSegment(sketch, "E159.38", {"start": v(-196.4, -71.79) * mm, "end": v(-196.4, -75.75) * mm});
            skLineSegment(sketch, "E159.39", {"start": v(-209.1, -71.79) * mm, "end": v(-196.4, -71.79) * mm});
            skLineSegment(sketch, "E159.40", {"start": v(-209.1, -71.79) * mm, "end": v(-209.1, -75.75) * mm});
            skLineSegment(sketch, "E160.MirrorCS", {"start": v(-70.58, -198.79) * mm, "end": v(-66.62, -198.79) * mm});
            skLineSegment(sketch, "E161.MirrorCS", {"start": v(-70.58, -122.59) * mm, "end": v(-66.61, -122.59) * mm});
            skLineSegment(sketch, "E162.MirrorCS", {"start": v(-70.58, -173.39) * mm, "end": v(-66.61, -173.39) * mm});
            skLineSegment(sketch, "E163.MirrorCS", {"start": v(-70.58, -135.29) * mm, "end": v(-66.61, -135.29) * mm});
            skLineSegment(sketch, "E164.MirrorCS", {"start": v(-70.58, -160.69) * mm, "end": v(-66.61, -160.69) * mm});
            skLineSegment(sketch, "E165.MirrorCS", {"start": v(-70.58, -186.09) * mm, "end": v(-66.61, -186.09) * mm});
            skLineSegment(sketch, "E166.MirrorCS", {"start": v(-70.58, -147.99) * mm, "end": v(-66.61, -147.99) * mm});
            skLineSegment(sketch, "E167.MirrorCS", {"start": v(-70.58, -97.19) * mm, "end": v(-66.61, -97.19) * mm});
            skLineSegment(sketch, "E168.MirrorCS", {"start": v(-70.58, -109.89) * mm, "end": v(-66.61, -109.89) * mm});
            skLineSegment(sketch, "E169.MirrorCS", {"start": v(-69.4, -84.49) * mm, "end": v(-66.61, -84.49) * mm});
            skLineSegment(sketch, "E170.MirrorCS", {"start": v(-70.58, -211.49) * mm, "end": v(-70.58, -198.79) * mm});
            skLineSegment(sketch, "E171.MirrorCS", {"start": v(-66.61, -109.89) * mm, "end": v(-66.61, -122.59) * mm});
            skLineSegment(sketch, "E172.MirrorCS", {"start": v(-70.58, -186.09) * mm, "end": v(-70.58, -173.39) * mm});
            skLineSegment(sketch, "E173.MirrorCS", {"start": v(-70.58, -122.59) * mm, "end": v(-70.58, -135.29) * mm});
            skLineSegment(sketch, "E174.MirrorCS", {"start": v(-69.4, -71.79) * mm, "end": v(-69.4, -84.49) * mm});
            skLineSegment(sketch, "E175.MirrorCS", {"start": v(-66.61, -97.19) * mm, "end": v(-66.61, -84.49) * mm});
            skLineSegment(sketch, "E176.MirrorCS", {"start": v(-70.58, -109.89) * mm, "end": v(-70.58, -97.19) * mm});
            skLineSegment(sketch, "E177.MirrorCS", {"start": v(-66.61, -160.69) * mm, "end": v(-66.61, -173.39) * mm});
            skLineSegment(sketch, "E178.MirrorCS", {"start": v(-70.58, -160.69) * mm, "end": v(-70.58, -147.99) * mm});
            skLineSegment(sketch, "E179.MirrorCS", {"start": v(-66.61, -147.99) * mm, "end": v(-66.61, -135.29) * mm});
            skLineSegment(sketch, "E180.MirrorCS", {"start": v(-66.62, -198.79) * mm, "end": v(-66.61, -186.09) * mm});
            skLineSegment(sketch, "E181.MirrorCS", {"start": v(-196.4, -211.49) * mm, "end": v(-196.4, -207.52) * mm});
            skLineSegment(sketch, "E182.MirrorCS", {"start": v(-272.6, -211.49) * mm, "end": v(-272.6, -207.52) * mm});
            skLineSegment(sketch, "E183.MirrorCS", {"start": v(-323.4, -211.49) * mm, "end": v(-323.4, -207.52) * mm});
            skLineSegment(sketch, "E184.MirrorCS", {"start": v(-259.9, -211.49) * mm, "end": v(-259.9, -207.52) * mm});
            skLineSegment(sketch, "E185.MirrorCS", {"start": v(-183.7, -211.49) * mm, "end": v(-183.7, -207.52) * mm});
            skLineSegment(sketch, "E186.MirrorCS", {"start": v(-171, -211.49) * mm, "end": v(-171, -207.52) * mm});
            skLineSegment(sketch, "E187.MirrorCS", {"start": v(-285.3, -211.49) * mm, "end": v(-285.3, -207.52) * mm});
            skLineSegment(sketch, "E188.MirrorCS", {"start": v(-158.3, -211.49) * mm, "end": v(-158.3, -207.52) * mm});
            skLineSegment(sketch, "E189.MirrorCS", {"start": v(-82.1, -211.49) * mm, "end": v(-82.1, -207.52) * mm});
            skLineSegment(sketch, "E190.MirrorCS", {"start": v(-298, -211.49) * mm, "end": v(-298, -207.52) * mm});
            skLineSegment(sketch, "E191.MirrorCS", {"start": v(-120.2, -211.49) * mm, "end": v(-120.2, -207.52) * mm});
            skLineSegment(sketch, "E192.MirrorCS", {"start": v(-145.6, -211.49) * mm, "end": v(-145.6, -207.52) * mm});
            skLineSegment(sketch, "E193.MirrorCS", {"start": v(-209.1, -211.49) * mm, "end": v(-209.1, -207.52) * mm});
            skLineSegment(sketch, "E194.MirrorCS", {"start": v(-221.8, -211.49) * mm, "end": v(-221.8, -207.52) * mm});
            skLineSegment(sketch, "E195.MirrorCS", {"start": v(-310.7, -211.49) * mm, "end": v(-310.7, -207.52) * mm});
            skLineSegment(sketch, "E196.MirrorCS", {"start": v(-132.9, -211.49) * mm, "end": v(-132.9, -207.52) * mm});
            skLineSegment(sketch, "E197.MirrorCS", {"start": v(-234.5, -211.49) * mm, "end": v(-234.5, -207.52) * mm});
            skLineSegment(sketch, "E198.MirrorCS", {"start": v(-247.2, -211.49) * mm, "end": v(-247.2, -207.52) * mm});
            skLineSegment(sketch, "E199.MirrorCS", {"start": v(-94.8, -211.49) * mm, "end": v(-94.8, -207.52) * mm});
            skLineSegment(sketch, "E200.MirrorCS", {"start": v(-158.3, -211.49) * mm, "end": v(-145.6, -211.49) * mm});
            skLineSegment(sketch, "E201.MirrorCS", {"start": v(-107.5, -207.52) * mm, "end": v(-120.2, -207.52) * mm});
            skLineSegment(sketch, "E202.MirrorCS", {"start": v(-209.1, -211.49) * mm, "end": v(-196.4, -211.49) * mm});
            skLineSegment(sketch, "E203.MirrorCS", {"start": v(-158.3, -207.52) * mm, "end": v(-171, -207.52) * mm});
            skLineSegment(sketch, "E204.MirrorCS", {"start": v(-247.2, -207.52) * mm, "end": v(-234.5, -207.52) * mm});
            skLineSegment(sketch, "E205.MirrorCS", {"start": v(-285.3, -211.49) * mm, "end": v(-272.6, -211.49) * mm});
            skLineSegment(sketch, "E206.MirrorCS", {"start": v(-336.1, -211.49) * mm, "end": v(-323.4, -211.49) * mm});
            skLineSegment(sketch, "E207.MirrorCS", {"start": v(-259.9, -207.52) * mm, "end": v(-272.6, -207.52) * mm});
            skLineSegment(sketch, "E208.MirrorCS", {"start": v(-120.2, -211.49) * mm, "end": v(-132.9, -211.49) * mm});
            skLineSegment(sketch, "E209.MirrorCS", {"start": v(-145.6, -207.52) * mm, "end": v(-132.9, -207.52) * mm});
            skLineSegment(sketch, "E210.MirrorCS", {"start": v(-69.4, -211.49) * mm, "end": v(-82.1, -211.49) * mm});
            skLineSegment(sketch, "E211.MirrorCS", {"start": v(-209.1, -207.52) * mm, "end": v(-221.8, -207.52) * mm});
            skLineSegment(sketch, "E212.MirrorCS", {"start": v(-221.8, -211.49) * mm, "end": v(-234.5, -211.49) * mm});
            skLineSegment(sketch, "E213.MirrorCS", {"start": v(-298, -207.52) * mm, "end": v(-285.3, -207.52) * mm});
            skLineSegment(sketch, "E214.MirrorCS", {"start": v(-94.8, -207.52) * mm, "end": v(-82.1, -207.52) * mm});
            skLineSegment(sketch, "E215.MirrorCS", {"start": v(-183.7, -211.49) * mm, "end": v(-171, -211.49) * mm});
            skLineSegment(sketch, "E216.MirrorCS", {"start": v(-310.7, -207.52) * mm, "end": v(-323.4, -207.52) * mm});
            skLineSegment(sketch, "E217.MirrorCS", {"start": v(-196.4, -207.52) * mm, "end": v(-183.7, -207.52) * mm});
            skLineSegment(sketch, "E218.MirrorCS", {"start": v(-107.5, -211.49) * mm, "end": v(-94.8, -211.49) * mm});
            skLineSegment(sketch, "E219.MirrorCS", {"start": v(-298, -211.49) * mm, "end": v(-310.7, -211.49) * mm});
            skLineSegment(sketch, "E220.MirrorCS", {"start": v(-247.2, -211.49) * mm, "end": v(-259.9, -211.49) * mm});
            skLineSegment(sketch, "E221", {"start": v(-336.1, -71.79) * mm, "end": v(-336.1, -135.29) * mm});
            skLineSegment(sketch, "E222", {"start": v(-107.5, -207.52) * mm, "end": v(-107.5, -211.49) * mm});
            skPoint(sketch, "E223.middle", {"position": v(-336.1, -141.64) * mm});
            skLineSegment(sketch, "E224", {"start": v(-332.12, -135.29) * mm, "end": v(-336.1, -135.29) * mm});
            skLineSegment(sketch, "E225", {"start": v(-332.12, -141.64) * mm, "end": v(-332.12, -135.29) * mm});
            skLineSegment(sketch, "E226.MirrorCS", {"start": v(-332.12, -141.64) * mm, "end": v(-332.12, -147.99) * mm});
            skLineSegment(sketch, "E227.MirrorCS", {"start": v(-332.12, -147.99) * mm, "end": v(-335.97, -147.99) * mm});
            skLineSegment(sketch, "E228", {"start": v(-336.1, -147.99) * mm, "end": v(-336.1, -211.49) * mm});
            skLineSegment(sketch, "E229", {"start": v(-335.97, -147.99) * mm, "end": v(-336.1, -147.99) * mm});
            skSolve(sketch);
        }
        {
            var Q0;
            Q0=makeQuery(id+"F4.imprint","IMPRINT",FACE,{"disambiguationData":[TD([[makeQuery(id+"F4.imprint","IMPRINT",EDGE,{"derivedFrom":sQuery(id+"F4.wireOp",EDGE,"E159.0")}),-1.0]])]});
            extrude(context, id + "F5", {"entities" : qUnion([Q0]), "depth" : 5 / 812.8 * mm});
        }
        {
            var Q0;
            Q0=makeQuery(id+"F1.opExtrude","CAP_FACE",FACE,{"disambiguationData":[OSD([sQuery(id+"F0.wireOp",EDGE,"E0"),sQuery(id+"F0.wireOp",EDGE,"E1.top"),sQuery(id+"F0.wireOp",EDGE,"E1.right"),sQuery(id+"F0.wireOp",EDGE,"E2.0.1.1"),sQuery(id+"F0.wireOp",EDGE,"E2.0.1.2"),sQuery(id+"F0.wireOp",EDGE,"E2.0.1.3"),sQuery(id+"F0.wireOp",EDGE,"E2.0.2.1"),sQuery(id+"F0.wireOp",EDGE,"E2.0.2.2"),sQuery(id+"F0.wireOp",EDGE,"E2.0.2.3"),sQuery(id+"F0.wireOp",EDGE,"E2.0.3.1"),sQuery(id+"F0.wireOp",EDGE,"E2.0.3.2"),sQuery(id+"F0.wireOp",EDGE,"E2.0.3.3"),sQuery(id+"F0.wireOp",EDGE,"E2.0.4.1"),sQuery(id+"F0.wireOp",EDGE,"E2.0.4.2"),sQuery(id+"F0.wireOp",EDGE,"E2.0.4.3"),sQuery(id+"F0.wireOp",EDGE,"E3"),sQuery(id+"F0.wireOp",EDGE,"E4"),sQuery(id+"F0.wireOp",EDGE,"E5"),sQuery(id+"F0.wireOp",EDGE,"E6"),sQuery(id+"F0.wireOp",EDGE,"E7"),sQuery(id+"F0.wireOp",EDGE,"E27"),sQuery(id+"F0.wireOp",EDGE,"E28.MirrorCS"),sQuery(id+"F0.wireOp",EDGE,"E21.MirrorCS"),sQuery(id+"F0.wireOp",EDGE,"E14.MirrorCS"),sQuery(id+"F0.wireOp",EDGE,"E29.MirrorCS"),sQuery(id+"F0.wireOp",EDGE,"E30.MirrorCS"),sQuery(id+"F0.wireOp",EDGE,"E31.MirrorCS"),sQuery(id+"F0.wireOp",EDGE,"E13.MirrorCS"),sQuery(id+"F0.wireOp",EDGE,"E20.MirrorCS"),sQuery(id+"F0.wireOp",EDGE,"E10.MirrorCS"),sQuery(id+"F0.wireOp",EDGE,"E32.MirrorCS"),sQuery(id+"F0.wireOp",EDGE,"E19.MirrorCS"),sQuery(id+"F0.wireOp",EDGE,"E33.MirrorCS"),sQuery(id+"F0.wireOp",EDGE,"E22.MirrorCS"),sQuery(id+"F0.wireOp",EDGE,"E12.MirrorCS"),sQuery(id+"F0.wireOp",EDGE,"E34.MirrorCS"),sQuery(id+"F0.wireOp",EDGE,"E16.MirrorCS"),sQuery(id+"F0.wireOp",EDGE,"E35.MirrorCS"),sQuery(id+"F0.wireOp",EDGE,"E36.MirrorCS"),sQuery(id+"F0.wireOp",EDGE,"E18.MirrorCS"),sQuery(id+"F0.wireOp",EDGE,"E37"),sQuery(id+"F0.wireOp",EDGE,"E45.MirrorCS"),sQuery(id+"F0.wireOp",EDGE,"E41.MirrorCS"),sQuery(id+"F0.wireOp",EDGE,"E43.MirrorCS"),sQuery(id+"F0.wireOp",EDGE,"E40.MirrorCS"),sQuery(id+"F0.wireOp",EDGE,"E44.MirrorCS"),sQuery(id+"F0.wireOp",EDGE,"E39.MirrorCS"),sQuery(id+"F0.wireOp",EDGE,"E42.MirrorCS"),sQuery(id+"F0.wireOp",EDGE,"E46.MirrorCS"),sQuery(id+"F0.wireOp",EDGE,"E47.MirrorCS"),sQuery(id+"F0.wireOp",EDGE,"E48.MirrorCS"),sQuery(id+"F0.wireOp",EDGE,"E52.MirrorCS"),sQuery(id+"F0.wireOp",EDGE,"E58.MirrorCS"),sQuery(id+"F0.wireOp",EDGE,"E60.MirrorCS"),sQuery(id+"F0.wireOp",EDGE,"E61.MirrorCS"),sQuery(id+"F0.wireOp",EDGE,"E62.MirrorCS"),sQuery(id+"F0.wireOp",EDGE,"E63.MirrorCS"),sQuery(id+"F0.wireOp",EDGE,"E64.MirrorCS"),sQuery(id+"F0.wireOp",EDGE,"E65.MirrorCS"),sQuery(id+"F0.wireOp",EDGE,"E66.MirrorCS"),sQuery(id+"F0.wireOp",EDGE,"E67.MirrorCS"),sQuery(id+"F0.wireOp",EDGE,"E68.MirrorCS"),sQuery(id+"F0.wireOp",EDGE,"E69.MirrorCS"),sQuery(id+"F0.wireOp",EDGE,"E70.MirrorCS"),sQuery(id+"F0.wireOp",EDGE,"E71.MirrorCS"),sQuery(id+"F0.wireOp",EDGE,"E72.MirrorCS"),sQuery(id+"F0.wireOp",EDGE,"E73.MirrorCS"),sQuery(id+"F0.wireOp",EDGE,"E74.MirrorCS"),sQuery(id+"F0.wireOp",EDGE,"E75.MirrorCS"),sQuery(id+"F0.wireOp",EDGE,"E76.MirrorCS"),sQuery(id+"F0.wireOp",EDGE,"E77.MirrorCS"),sQuery(id+"F0.wireOp",EDGE,"E78.MirrorCS"),sQuery(id+"F0.wireOp",EDGE,"E79.MirrorCS"),sQuery(id+"F0.wireOp",EDGE,"E81.MirrorCS"),sQuery(id+"F0.wireOp",EDGE,"E82.MirrorCS"),sQuery(id+"F0.wireOp",EDGE,"E83.MirrorCS"),sQuery(id+"F0.wireOp",EDGE,"E84.MirrorCS"),sQuery(id+"F0.wireOp",EDGE,"E85.MirrorCS"),sQuery(id+"F0.wireOp",EDGE,"E86.MirrorCS"),sQuery(id+"F0.wireOp",EDGE,"E87.MirrorCS"),sQuery(id+"F0.wireOp",EDGE,"E88.MirrorCS"),sQuery(id+"F0.wireOp",EDGE,"E89.MirrorCS"),sQuery(id+"F0.wireOp",EDGE,"E90.MirrorCS"),sQuery(id+"F0.wireOp",EDGE,"E91.MirrorCS")])],"isStart":false});
            var sketch = newSketch(context, id + "F6", { "sketchPlane" : qUnion([Q0])});
            skLineSegment(sketch, "E230", {"start": v(-65.42, 55.21) * mm, "end": v(-65.42, 63.95) * mm});
            skLineSegment(sketch, "E231.bottom", {"start": v(-65.42, 63.95) * mm, "end": v(-5.9, 63.95) * mm});
            skLineSegment(sketch, "E231.top", {"start": v(-65.42, -67.82) * mm, "end": v(-5.9, -67.82) * mm});
            skLineSegment(sketch, "E231.left", {"start": v(-65.42, 63.95) * mm, "end": v(-65.42, -67.82) * mm});
            skLineSegment(sketch, "E231.right", {"start": v(66.34, 63.95) * mm, "end": v(66.34, -67.82) * mm});
            skLineSegment(sketch, "E232.0", {"start": v(-5.9, -67.82) * mm, "end": v(-5.9, -71.79) * mm});
            skLineSegment(sketch, "E233.0", {"start": v(6.8, -67.82) * mm, "end": v(6.8, -71.79) * mm});
            skLineSegment(sketch, "E234", {"start": v(-5.9, -71.79) * mm, "end": v(-5.9, -67.82) * mm});
            skLineSegment(sketch, "E235.MirrorCS", {"start": v(-5.9, 67.91) * mm, "end": v(-5.9, 63.95) * mm});
            skLineSegment(sketch, "E236.MirrorCS", {"start": v(6.8, 63.95) * mm, "end": v(6.8, 67.91) * mm});
            skLineSegment(sketch, "E237.MirrorCS", {"start": v(-5.9, 67.91) * mm, "end": v(-5.9, 71.88) * mm});
            skLineSegment(sketch, "E238.MirrorCS", {"start": v(6.8, 71.88) * mm, "end": v(6.8, 67.91) * mm});
            skLineSegment(sketch, "E239", {"start": v(-5.9, 71.88) * mm, "end": v(6.8, 71.88) * mm});
            skLineSegment(sketch, "E240.MirrorCS", {"start": v(-5.9, -71.79) * mm, "end": v(-5.9, -75.75) * mm});
            skLineSegment(sketch, "E241.MirrorCS", {"start": v(6.8, -75.75) * mm, "end": v(6.8, -71.79) * mm});
            skLineSegment(sketch, "E242", {"start": v(-5.9, -75.75) * mm, "end": v(6.8, -75.75) * mm});
            skLineSegment(sketch, "E243", {"start": v(6.8, 63.95) * mm, "end": v(66.34, 63.95) * mm});
            skLineSegment(sketch, "E244", {"start": v(6.8, -67.82) * mm, "end": v(66.34, -67.82) * mm});
            skSolve(sketch);
        }
        {
            var Q0;
            {var subQ2=makeQuery(id+"F1.opExtrude","CAP_EDGE",EDGE,{"disambiguationData":[OSD([sQuery(id+"F0.wireOp",EDGE,"E62.MirrorCS")])],"isStart":false});Q0=makeQuery(id+"F6.imprint","IMPRINT",FACE,{"disambiguationData":[TD([[makeQuery(id+"F6.imprint","IMPRINT",EDGE,{"derivedFrom":subQ2}),1.0]])]});}
            var Q1;
            {var subQ1=sQuery(id+"F6.wireOp",EDGE,"E234");Q1=makeQuery(id+"F6.imprint","IMPRINT",FACE,{"disambiguationData":[TD([[makeQuery(id+"F6.imprint","IMPRINT",EDGE,{"derivedFrom":subQ1}),1.0]])]});}
            var Q2;
            {var subQ1=sQuery(id+"F6.wireOp",EDGE,"E235.MirrorCS");Q2=makeQuery(id+"F6.imprint","IMPRINT",FACE,{"disambiguationData":[TD([[makeQuery(id+"F6.imprint","IMPRINT",EDGE,{"derivedFrom":subQ1}),-1.0]])]});}
            extrude(context, id + "F7", {"entities" : qUnion([Q0, Q1, Q2]), "depth" : 5 / 812.8 * mm});
        }
    });
